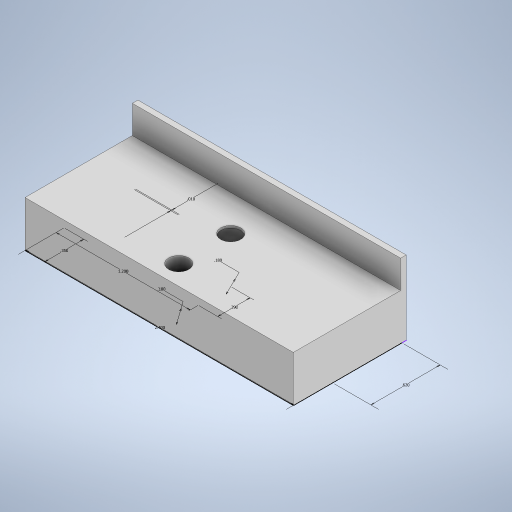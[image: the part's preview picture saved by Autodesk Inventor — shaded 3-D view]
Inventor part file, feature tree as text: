
AUTODESK INVENTOR PART (.ipt)
format: ipt  version: 2024.2 (Build 282272000, 272)  size: 268,288 bytes
history: native  units: in
note: dims shown in document units (in); Inventor stores cm internally (conversion verified against a paired STEP export)
features: extrude x5, sketch x3
ambient origin geometry x8: Origin, YZ Plane, XZ Plane, XY Plane, X Axis, Y Axis, Z Axis, Center Point
bodies: Solid1 (feature_tree)
feature tree (8):
  sketch  "Sketch1"  dims[d0=1.2in d1=2.4in]
  extrude  "Extrusion1"  Depth=2.4in
  extrude  "Extrusion2"  Depth=0.01in
  extrude  "Extrusion3"  Depth=0.175in
  extrude  "Extrusion4"  Depth=0.41in TaperAngle=0.0deg
  extrude  "Extrusion5"  Depth=0.66in TaperAngle=0.0deg
  sketch  "Sketch2"  dims[d2=0.62in d3=0.01in]
  sketch  "Sketch3"  dims[d4=0.29in d5=0.18in d6=0.41in d7=0.0in d8=0.66in d9=0.0in d10=0.29in d11=0.3in d12=0.39in d13=0.0in d14=0.35in d15=0.18in d16=0.41in d17=0.0in d18=0.197in d19=0.197in d20=0.0796in d21=0.0796in d22=0.175in d23=0.0in]
